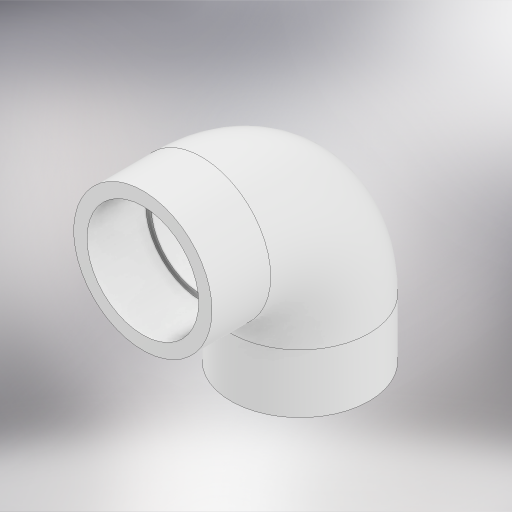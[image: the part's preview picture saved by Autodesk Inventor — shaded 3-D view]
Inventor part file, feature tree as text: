
AUTODESK INVENTOR PART (.ipt)
format: ipt  version: 2023 (Build 270158000, 158)  size: 352,256 bytes
history: native  units: mm
features: sketch x5, revolve x2, extrude x2
ambient origin geometry x8: Origin, YZ Plane, XZ Plane, XY Plane, X Axis, Y Axis, Z Axis, Center Point
bodies: Body1 (feature_tree)
feature tree (9):
  sketch  "Boceto6"  dims[d12=33.0mm d13=40.0mm]
  revolve  "Revolución1"  [1 undecoded]
  extrude  "Extrusión4"  Depth=16.5mm
  extrude  "Extrusión5"  Depth=16.5mm
  revolve  "Revolución2"  [1 undecoded]
  sketch  "Boceto7"  dims[d14=16.5mm d15=33.0mm]
  sketch  "Boceto8"  dims[d16=40.0mm d17=16.5mm]
  sketch  "Boceto9"  dims[d18=90.0deg d19=26.65mm]
  sketch  "Boceto10"  dims[d20=14.0mm d21=0.0mm d22=26.65mm d23=14.0mm d24=0.0mm d25=24.0mm d26=90.0deg]
note: 2 required parameter values undecoded (feature->parameter linkage not recoverable at this tier; creation-order binding heuristic only, values carry confidence <= 0.55)
